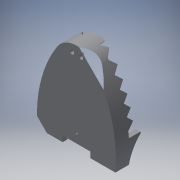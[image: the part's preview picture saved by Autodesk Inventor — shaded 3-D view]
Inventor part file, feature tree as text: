
AUTODESK INVENTOR PART (.ipt)
format: ipt  version: 2016 (Build 200138000, 138)  size: 524,800 bytes
history: native  units: in
note: dims shown in document units (in); Inventor stores cm internally (conversion verified against a paired STEP export)
features: sketch x28, extrude x27, other x12, plane x12, projected_geometry x8, reference x2, fillet x1
ambient origin geometry x8: Origin, YZ Plane, XZ Plane, XY Plane, X Axis, Y Axis, Z Axis, Center Point
bodies: Solid1 (feature_tree)
feature tree (90):
  extrude  "Extrusion1"  Depth=1.0in
  extrude  "Extrusion2"  Depth=0.3937in TaperAngle=0.0deg
  extrude  "Extrusion3"  Depth=1.0in
  extrude  "Extrusion4"  Depth=1.0in TaperAngle=0.0deg
  sketch  "Sketch5"  dims[d12=1.0in d13=0.0in d15=0.5in]
  other  "Work Point1"
  other  "Work Point2"
  other  "Work Point3"
  other  "Work Point4"
  other  "Work Point5"
  other  "Work Point6"
  other  "Work Point7"
  other  "Work Point8"
  other  "Work Point9"
  other  "Work Point10"
  other  "Work Point11"
  other  "Work Point12"
  plane  "Work Plane1"
  plane  "Work Plane2"
  plane  "Work Plane3"
  plane  "Work Plane4"
  plane  "Work Plane5"
  plane  "Work Plane6"
  sketch  "Sketch6"  dims[d16=2.3622in d18=0.45in d19=0.3937in d21=1.0in d23=0.25in]
  sketch  "Sketch7"  dims[d24=0.5in d25=0.25in]
  sketch  "Sketch8"  dims[d26=0.25in d27=0.5in d28=0.25in d29=0.25in d30=0.5in d31=0.25in]
  sketch  "Sketch9"  dims[d32=0.25in d33=0.5in d34=0.25in d35=0.25in d36=0.5in d37=0.25in]
  sketch  "Sketch10"  dims[d38=0.25in d39=0.5in d40=0.25in d44=1.0in d45=0.0in]
  sketch  "Sketch11"  dims[d46=1.0in d47=0.0in d48=1.0in d49=0.0in]
  extrude  "Extrusion5"  Depth=0.5in
  extrude  "Extrusion6"  Depth=0.3937in
  extrude  "Extrusion7"  Depth=0.25in
  extrude  "Extrusion8"  Depth=0.25in
  extrude  "Extrusion9"  Depth=0.25in
  extrude  "Extrusion10"  Depth=1.0in TaperAngle=0.0deg
  plane  "Work Plane7"
  plane  "Work Plane8"
  plane  "Work Plane9"
  plane  "Work Plane10"
  plane  "Work Plane11"
  plane  "Work Plane12"
  sketch  "Sketch13"  dims[d50=1.0in d51=0.0in d52=1.0in d53=0.0in]
  sketch  "Sketch14"  dims[d54=1.0in d55=0.0in d56=0.25in]
  sketch  "Sketch15"  dims[d57=0.5in d58=0.25in]
  sketch  "Sketch16"  dims[d59=0.25in d60=0.5in d61=0.25in d62=0.25in d63=0.5in d64=0.25in]
  sketch  "Sketch17"  dims[d65=0.25in d66=0.5in d67=0.25in d68=0.25in d69=0.5in d70=0.25in]
  sketch  "Sketch18"  dims[d71=0.25in d72=0.5in d73=0.25in d74=1.0in d75=0.0in]
  extrude  "Extrusion11"  Depth=1.0in TaperAngle=0.0deg
  extrude  "Extrusion12"  Depth=1.0in TaperAngle=0.0deg
  extrude  "Extrusion13"  Depth=0.25in
  extrude  "Extrusion14"  Depth=0.25in
  extrude  "Extrusion15"  Depth=0.25in
  extrude  "Extrusion16"  Depth=0.25in
  extrude  "Extrusion17"  Depth=1.0in TaperAngle=0.0deg
  extrude  "Extrusion18"  Depth=1.0in TaperAngle=0.0deg
  extrude  "Extrusion19"  Depth=1.0in TaperAngle=0.0deg
  extrude  "Extrusion20"  Depth=1.0in TaperAngle=0.0deg
  extrude  "Extrusion21"  Depth=32534.0in TaperAngle=0.0deg
  extrude  "Extrusion22"  Depth=4.0in TaperAngle=0.0deg
  extrude  "Extrusion23"  Depth=0.6in
  extrude  "Extrusion24"  Depth=0.25in
  extrude  "Extrusion25"  Depth=1.0in TaperAngle=0.0deg
  fillet  "Fillet1"  Radius=0.2953in
  extrude  "Extrusion26"  Depth=0.1969in
  extrude  "Extrusion27"  Depth=0.3937in
  sketch  "Sketch1"  dims[d0=4.5in d1=1.0in]
  reference  "Reference1"
  sketch  "Sketch2"  dims[d2=0.1969in d3=0.0in d4=0.3937in d5=0.0in]
  projected_geometry  "Projected Loop1"
  sketch  "Sketch3"  dims[d6=0.9843in d7=1.0in]
  sketch  "Sketch4"  dims[d8=4.0in d9=0.0in d10=1.0in d11=0.0in]
  projected_geometry  "Projected Loop2"
  projected_geometry  "Projected Loop3"
  sketch  "Sketch19"  dims[d76=1.0in d77=0.0in d78=1.0in d79=0.0in]
  projected_geometry  "Projected Loop4"
  sketch  "Sketch20"  dims[d80=1.0in d81=0.0in d82=1.0in d83=0.0in]
  reference  "Reference2"
  sketch  "Sketch21"  dims[d84=1.0in d85=0.0in d86=1.0in d87=0.0in]
  sketch  "Sketch22"  dims[d88=4.0in d89=0.0in d90=32534.0in d91=0.0in]
  sketch  "Sketch23"  dims[d92=4.0in d93=1.0in d94=0.0in d95=0.0in d96=4.0in d97=0.0in]
  projected_geometry  "Projected Loop5"
  sketch  "Sketch24"  dims[d98=4.0in d99=0.0in d100=0.6in]
  projected_geometry  "Projected Loop6"
  sketch  "Sketch25"  dims[d101=1.2in d102=0.25in]
  sketch  "Sketch26"  dims[d103=4.0in d104=0.0in d105=1.0in d106=0.0in d107=0.2953in d108=0.0in]
  projected_geometry  "Projected Loop7"
  sketch  "Sketch27"  dims[d109=0.0394in d110=0.1969in]
  projected_geometry  "Projected Loop8"
  sketch  "Sketch28"  dims[d111=0.1969in d112=0.3937in]
  sketch  "Sketch29"  dims[d113=0.19in d114=0.19in d115=1.0in d116=0.0in d117=0.0984in d118=1.0in d119=0.0in]
